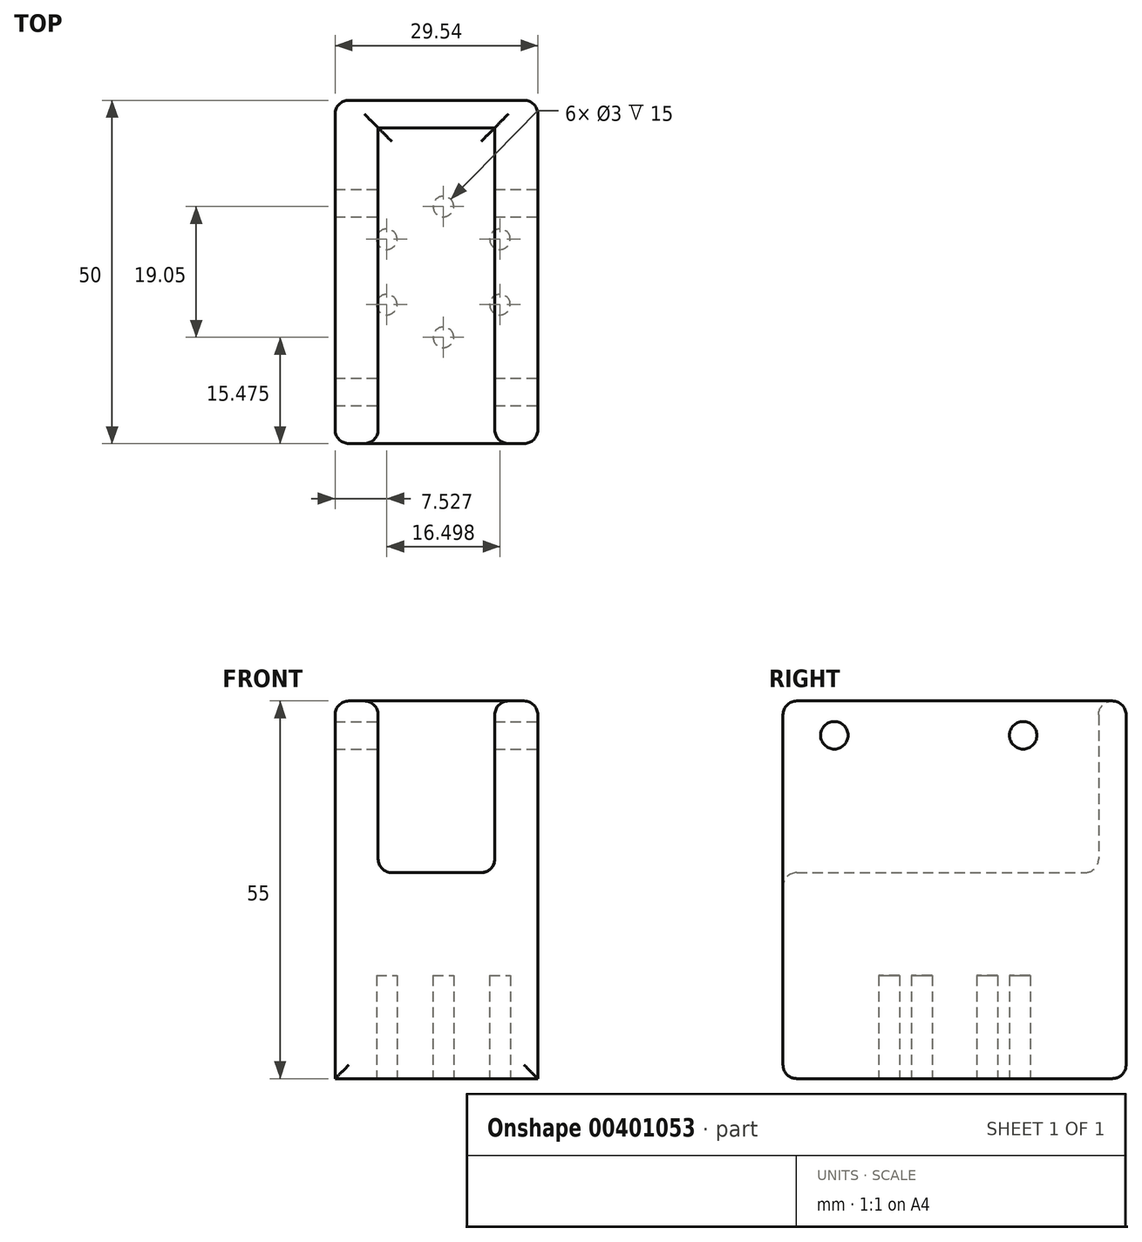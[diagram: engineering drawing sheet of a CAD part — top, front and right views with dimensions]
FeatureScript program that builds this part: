
annotation { "Feature Type Name" : "Feature", "Feature Type Description" : "" }
export const myFeature = defineFeature(function(context is Context, id is Id, definition is map)
    precondition{}
    {
        {
            var Q0;
            Q0=qCreatedBy(makeId("Top.planeOp"),FACE);
            var sketch = newSketch(context, id + "F0", { "sketchPlane" : qUnion([Q0])});
            skLineSegment(sketch, "E0.left", {"start": v(-8.5, 0) * mm, "end": v(-8.5, 21) * mm});
            skLineSegment(sketch, "E0.right", {"start": v(8.5, 0) * mm, "end": v(8.5, 21) * mm});
            skLineSegment(sketch, "E1", {"start": v(-8.5, 21) * mm, "end": v(8.5, 21) * mm});
            skLineSegment(sketch, "E2", {"start": v(8.5, 0) * mm, "end": v(8.5, -23.51) * mm});
            skLineSegment(sketch, "E3", {"start": v(-8.5, 0) * mm, "end": v(-8.5, -23.51) * mm});
            skLineSegment(sketch, "E4", {"start": v(14.77, -13.51) * mm, "end": v(14.77, -20.17) * mm});
            skLineSegment(sketch, "E5.bottom", {"start": v(-25, 25) * mm, "end": v(25, 25) * mm});
            skLineSegment(sketch, "E5.top", {"start": v(-25, -25) * mm, "end": v(25, -25) * mm});
            skLineSegment(sketch, "E5.left", {"start": v(-25, 25) * mm, "end": v(-25, -25) * mm});
            skLineSegment(sketch, "E5.right", {"start": v(25, 25) * mm, "end": v(25, -25) * mm});
            skLineSegment(sketch, "E6", {"start": v(-14.77, -20.17) * mm, "end": v(-14.77, -25) * mm});
            skLineSegment(sketch, "E7", {"start": v(14.77, -20.17) * mm, "end": v(14.77, -25) * mm});
            skLineSegment(sketch, "E8", {"start": v(-8.5, -23.51) * mm, "end": v(-8.5, -25) * mm});
            skLineSegment(sketch, "E9", {"start": v(8.5, -23.51) * mm, "end": v(8.5, -25) * mm});
            skLineSegment(sketch, "E10", {"start": v(14.77, -13.51) * mm, "end": v(14.77, 25) * mm});
            skLineSegment(sketch, "E11", {"start": v(-14.77, -25) * mm, "end": v(-14.77, 25) * mm});
            skSolve(sketch);
        }
        {
            var Q0;
            {var subQ1=sQuery(id+"F0.wireOp",EDGE,"E0.left");Q0=makeQuery(id+"F0.imprint","IMPRINT",FACE,{"disambiguationData":[TD([[makeQuery(id+"F0.imprint","IMPRINT",EDGE,{"derivedFrom":subQ1}),1.0]])]});}
            var Q1;
            {var subQ3=sQuery(id+"F0.wireOp",EDGE,"bu9vcPg2-ATEx-ZIaZ-XLWS-YSRfaz45pnAs");Q1=makeQuery(id+"F0.imprint","IMPRINT",FACE,{"disambiguationData":[TD([[makeQuery(id+"F0.imprint","IMPRINT",EDGE,{"derivedFrom":subQ3}),1.0]])]});}
            var Q2;
            {var subQ4=sQuery(id+"F0.wireOp",EDGE,"E4");Q2=makeQuery(id+"F0.imprint","IMPRINT",FACE,{"disambiguationData":[TD([[makeQuery(id+"F0.imprint","IMPRINT",EDGE,{"derivedFrom":subQ4}),-1.0]])]});}
            extrude(context, id + "F1", {"entities" : qUnion([Q0, Q1, Q2]), "depth" : 25 * mm, "offsetDistance" : 25 * mm});
        }
        {
            var Q0;
            Q0=makeQuery(id+"F0.imprint","IMPRINT",FACE,{"disambiguationData":[TD([[makeQuery(id+"F0.imprint","IMPRINT",EDGE,{"derivedFrom":sQuery(id+"F0.wireOp",EDGE,"JjuJuUTR-XIjw-p3LP-uiln-kea8M6GB0FUg.right")}),-1.0]])]});
            var Q1;
            {var subQ4=sQuery(id+"F0.wireOp",EDGE,"E0.left");Q1=makeQuery(id+"F0.imprint","IMPRINT",FACE,{"disambiguationData":[TD([[makeQuery(id+"F0.imprint","IMPRINT",EDGE,{"derivedFrom":subQ4}),-1.0]])]});}
            var Q2;
            Q2=makeQuery(id+"F0.imprint","IMPRINT",FACE,{"disambiguationData":[TD([[makeQuery(id+"F0.imprint","IMPRINT",EDGE,{"derivedFrom":sQuery(id+"F0.wireOp",EDGE,"JjuJuUTR-XIjw-p3LP-uiln-kea8M6GB0FUg.left")}),1.0]])]});
            var Q3;
            {var subQ1=sQuery(id+"F0.wireOp",EDGE,"E0.left");Q3=makeQuery(id+"F0.imprint","IMPRINT",FACE,{"disambiguationData":[TD([[makeQuery(id+"F0.imprint","IMPRINT",EDGE,{"derivedFrom":subQ1}),1.0]])]});}
            var Q4;
            {var subQ3=sQuery(id+"F0.wireOp",EDGE,"bu9vcPg2-ATEx-ZIaZ-XLWS-YSRfaz45pnAs");Q4=makeQuery(id+"F0.imprint","IMPRINT",FACE,{"disambiguationData":[TD([[makeQuery(id+"F0.imprint","IMPRINT",EDGE,{"derivedFrom":subQ3}),1.0]])]});}
            var Q5;
            {var subQ4=sQuery(id+"F0.wireOp",EDGE,"E4");Q5=makeQuery(id+"F0.imprint","IMPRINT",FACE,{"disambiguationData":[TD([[makeQuery(id+"F0.imprint","IMPRINT",EDGE,{"derivedFrom":subQ4}),-1.0]])]});}
            extrude(context, id + "F2", {"entities" : qUnion([Q0, Q1, Q2, Q3, Q4, Q5]), "operationType" : NewBodyOperationType.ADD, "oppositeDirection" : true, "depth" : 5 * mm, "offsetDistance" : 25 * mm});
        }
        {
            var Q0;
            Q0=makeQuery(id+"F2.opExtrude","CAP_FACE",FACE,{"disambiguationData":[OSD([sQuery(id+"F0.wireOp",EDGE,"E5.bottom"),sQuery(id+"F0.wireOp",EDGE,"E5.top"),sQuery(id+"F0.wireOp",EDGE,"E5.left"),sQuery(id+"F0.wireOp",EDGE,"E5.right")])],"isStart":false});
            extrude(context, id + "F3", {"entities" : qUnion([Q0]), "operationType" : NewBodyOperationType.ADD, "depth" : 25 * mm, "offsetDistance" : 25 * mm});
        }
        {
            var Q0;
            {var subQ0=sQuery(id+"F0.wireOp",EDGE,"E10");var subQ1=sQuery(id+"F0.wireOp",EDGE,"E7");var subQ2=sQuery(id+"F0.wireOp",EDGE,"E4");Q0=makeQuery(id+"F3.boolean.opBoolean","MERGE",FACE,{"derivedFrom":[makeQuery(id+"F2.boolean.opBoolean","MERGE",FACE,{"derivedFrom":[makeQuery(id+"F1.opExtrude","SWEPT_FACE",FACE,{"disambiguationData":[OSD([subQ2,subQ1,subQ0])]}),makeQuery(id+"F2.opExtrude","SWEPT_FACE",FACE,{"disambiguationData":[OSD([subQ2,subQ1,subQ0])]})]}),makeQuery(id+"F3.opExtrude","SWEPT_FACE",FACE,{"disambiguationData":[OSD([subQ2,subQ1,subQ0])]})]});}
            var sketch = newSketch(context, id + "F4", { "sketchPlane" : qUnion([Q0])});
            skCircle(sketch, "E12", {"center": v(10, 20) * mm, "radius": 2 * mm});
            skSolve(sketch);
        }
        {
            var Q0;
            Q0=makeQuery(id+"F4.imprint","IMPRINT",FACE,{"disambiguationData":[TD([[makeQuery(id+"F4.imprint","IMPRINT",EDGE,{"derivedFrom":sQuery(id+"F4.wireOp",EDGE,"E12")}),1.0]])]});
            extrude(context, id + "F5", {"entities" : qUnion([Q0]), "operationType" : NewBodyOperationType.REMOVE, "endBound" : BoundingType.THROUGH_ALL, "oppositeDirection" : true, "depth" : 25 * mm, "offsetDistance" : 25 * mm});
        }
        {
            var Q0;
            Q0=makeQuery(id+"F1.opExtrude","SWEPT_FACE",FACE,{"disambiguationData":[OSD([sQuery(id+"F0.wireOp",EDGE,"E4"),sQuery(id+"F0.wireOp",EDGE,"E7")])]});
            var sketch = newSketch(context, id + "F6", { "sketchPlane" : qUnion([Q0])});
            skCircle(sketch, "E13", {"center": v(-17.51, 20) * mm, "radius": 2 * mm});
            skSolve(sketch);
        }
        {
            var Q0;
            Q0=makeQuery(id+"F6.imprint","IMPRINT",FACE,{"disambiguationData":[TD([[makeQuery(id+"F6.imprint","IMPRINT",EDGE,{"derivedFrom":sQuery(id+"F6.wireOp",EDGE,"E13")}),1.0]])]});
            extrude(context, id + "F7", {"entities" : qUnion([Q0]), "operationType" : NewBodyOperationType.REMOVE, "endBound" : BoundingType.THROUGH_ALL, "oppositeDirection" : true, "depth" : 25 * mm, "offsetDistance" : 25 * mm});
        }
        {
            var Q0;
            {var subQ0=sQuery(id+"F0.wireOp",EDGE,"E5.left");Q0=makeQuery(id+"F3.boolean.opBoolean","MERGE",FACE,{"derivedFrom":[makeQuery(id+"F2.opExtrude","SWEPT_FACE",FACE,{"disambiguationData":[OSD([subQ0])]}),makeQuery(id+"F3.opExtrude","SWEPT_FACE",FACE,{"disambiguationData":[OSD([subQ0])]})]});}
            var Q1;
            Q1=makeQuery(id+"F1.opExtrude","SWEPT_FACE",FACE,{"disambiguationData":[OSD([sQuery(id+"F0.wireOp",EDGE,"cDZ9KRWL-NaUr-2VU4-3PM3-z0CJBz9VJkfU")])]});
            var Q2;
            Q2=makeQuery(id+"F1.opExtrude","CAP_FACE",FACE,{"disambiguationData":[OSD([sQuery(id+"F0.wireOp",EDGE,"E0.left"),sQuery(id+"F0.wireOp",EDGE,"E0.right"),sQuery(id+"F0.wireOp",EDGE,"JjuJuUTR-XIjw-p3LP-uiln-kea8M6GB0FUg.left"),sQuery(id+"F0.wireOp",EDGE,"JjuJuUTR-XIjw-p3LP-uiln-kea8M6GB0FUg.right"),sQuery(id+"F0.wireOp",EDGE,"E1"),sQuery(id+"F0.wireOp",EDGE,"E2"),sQuery(id+"F0.wireOp",EDGE,"E3"),sQuery(id+"F0.wireOp",EDGE,"bu9vcPg2-ATEx-ZIaZ-XLWS-YSRfaz45pnAs"),sQuery(id+"F0.wireOp",EDGE,"E4"),sQuery(id+"F0.wireOp",EDGE,"Vo7dQ3KN-mIEG-PosT-gOyy-nh5kmKhcDDbw"),sQuery(id+"F0.wireOp",EDGE,"1lZYz93q-oRxk-5rwe-9EyB-DwqBscyPRtee"),sQuery(id+"F0.wireOp",EDGE,"E5.bottom"),sQuery(id+"F0.wireOp",EDGE,"E5.top"),sQuery(id+"F0.wireOp",EDGE,"T2WauGqo-VF5D-FPXN-nkIz-Tow7OxX6UALv"),sQuery(id+"F0.wireOp",EDGE,"Eb9nccsw-4lB1-myll-ZeQB-EgrNam2AgwgF"),sQuery(id+"F0.wireOp",EDGE,"E6"),sQuery(id+"F0.wireOp",EDGE,"E7"),sQuery(id+"F0.wireOp",EDGE,"E8"),sQuery(id+"F0.wireOp",EDGE,"E9"),sQuery(id+"F0.wireOp",EDGE,"Qe85SMm2-kEps-NXLD-GZTa-d0BaLbSc7Nne"),sQuery(id+"F0.wireOp",EDGE,"cDZ9KRWL-NaUr-2VU4-3PM3-z0CJBz9VJkfU")])],"isStart":false});
            var Q3;
            {var subQ0=sQuery(id+"F0.wireOp",EDGE,"E5.bottom");Q3=makeQuery(id+"F3.boolean.opBoolean","MERGE",FACE,{"derivedFrom":[makeQuery(id+"F2.boolean.opBoolean","MERGE",FACE,{"derivedFrom":[makeQuery(id+"F1.opExtrude","SWEPT_FACE",FACE,{"disambiguationData":[OSD([subQ0])]}),makeQuery(id+"F2.opExtrude","SWEPT_FACE",FACE,{"disambiguationData":[OSD([subQ0])]})]}),makeQuery(id+"F3.opExtrude","SWEPT_FACE",FACE,{"disambiguationData":[OSD([subQ0])]})]});}
            var Q4;
            Q4=makeQuery(id+"F1.opExtrude","SWEPT_FACE",FACE,{"disambiguationData":[OSD([sQuery(id+"F0.wireOp",EDGE,"Qe85SMm2-kEps-NXLD-GZTa-d0BaLbSc7Nne")])]});
            var Q5;
            {var subQ0=sQuery(id+"F0.wireOp",EDGE,"E5.top");Q5=makeQuery(id+"F3.boolean.opBoolean","MERGE",FACE,{"derivedFrom":[makeQuery(id+"F2.boolean.opBoolean","MERGE",FACE,{"derivedFrom":[makeQuery(id+"F1.opExtrude","SWEPT_FACE",FACE,{"disambiguationData":[OSD([subQ0]),TDD([makeQuery(id+"F0.imprint","IMPRINT",EDGE,{"disambiguationData":[TD([[makeQuery(id+"F0.imprint","INTERSECT",VERTEX,{"derivedFrom":[subQ0,sQuery(id+"F0.wireOp",EDGE,"E6")]}),-1.0]])],"derivedFrom":subQ0})])]}),makeQuery(id+"F1.opExtrude","SWEPT_FACE",FACE,{"disambiguationData":[OSD([subQ0]),TDD([makeQuery(id+"F0.imprint","IMPRINT",EDGE,{"disambiguationData":[TD([[makeQuery(id+"F0.imprint","INTERSECT",VERTEX,{"derivedFrom":[subQ0,sQuery(id+"F0.wireOp",EDGE,"E7")]}),1.0]])],"derivedFrom":subQ0})])]}),makeQuery(id+"F2.opExtrude","SWEPT_FACE",FACE,{"disambiguationData":[OSD([subQ0])]})]}),makeQuery(id+"F3.opExtrude","SWEPT_FACE",FACE,{"disambiguationData":[OSD([subQ0])]})]});}
            var Q6;
            {var subQ1=sQuery(id+"F0.wireOp",EDGE,"E5.top");var subQ2=sQuery(id+"F0.wireOp",EDGE,"E5.bottom");var subQ3=sQuery(id+"F0.wireOp",EDGE,"E5.left");Q6=makeQuery(id+"F2.boolean.opBoolean","SPLIT",FACE,{"disambiguationData":[TD([makeQuery(id+"F1.opExtrude","SWEPT_FACE",FACE,{"disambiguationData":[OSD([sQuery(id+"F0.wireOp",EDGE,"cDZ9KRWL-NaUr-2VU4-3PM3-z0CJBz9VJkfU")])]})])],"derivedFrom":makeQuery(id+"F2.opExtrude","CAP_FACE",FACE,{"disambiguationData":[OSD([subQ2,subQ1,subQ3,sQuery(id+"F0.wireOp",EDGE,"E5.right")])],"isStart":true})});}
            var Q7;
            {var subQ0=sQuery(id+"F0.wireOp",EDGE,"E5.bottom");var subQ1=sQuery(id+"F0.wireOp",EDGE,"E5.right");var subQ3=sQuery(id+"F0.wireOp",EDGE,"E5.top");Q7=makeQuery(id+"F2.boolean.opBoolean","SPLIT",FACE,{"disambiguationData":[TD([makeQuery(id+"F1.opExtrude","SWEPT_FACE",FACE,{"disambiguationData":[OSD([sQuery(id+"F0.wireOp",EDGE,"Qe85SMm2-kEps-NXLD-GZTa-d0BaLbSc7Nne")])]})])],"derivedFrom":makeQuery(id+"F2.opExtrude","CAP_FACE",FACE,{"disambiguationData":[OSD([subQ0,subQ3,sQuery(id+"F0.wireOp",EDGE,"E5.left"),subQ1])],"isStart":true})});}
            fillet(context, id + "F8", {"entities" : qUnion([Q0, Q1, Q2, Q3, Q4, Q5, Q6, Q7]), "radius" : 2 * mm, "tangentPropagation" : true, "allowEdgeOverflow" : false});
        }
        {
            var Q0;
            Q0=makeQuery(id+"F3.opExtrude","CAP_FACE",FACE,{"disambiguationData":[OSD([sQuery(id+"F0.wireOp",EDGE,"E5.bottom"),sQuery(id+"F0.wireOp",EDGE,"E5.top"),sQuery(id+"F0.wireOp",EDGE,"E5.left"),sQuery(id+"F0.wireOp",EDGE,"E5.right")])],"isStart":false});
            var sketch = newSketch(context, id + "F9", { "sketchPlane" : qUnion([Q0])});
            skCircle(sketch, "E14", {"center": v(1, 9.53) * mm, "radius": 1.5 * mm});
            skCircle(sketch, "E15.1.0", {"center": v(-7.24, 4.76) * mm, "radius": 1.5 * mm});
            skCircle(sketch, "E15.2.0", {"center": v(-7.24, -4.76) * mm, "radius": 1.5 * mm});
            skCircle(sketch, "E15.3.0", {"center": v(1, -9.53) * mm, "radius": 1.5 * mm});
            skCircle(sketch, "E15.4.0", {"center": v(9.25, -4.76) * mm, "radius": 1.5 * mm});
            skCircle(sketch, "E15.5.0", {"center": v(9.25, 4.76) * mm, "radius": 1.5 * mm});
            skPoint(sketch, "E15.center", {"position": v(1, 0) * mm});
            skSolve(sketch);
        }
        {
            var Q0;
            Q0=makeQuery(id+"F9.imprint","IMPRINT",FACE,{"disambiguationData":[TD([[makeQuery(id+"F9.imprint","IMPRINT",EDGE,{"derivedFrom":sQuery(id+"F9.wireOp",EDGE,"E15.4.0")}),1.0]])]});
            var Q1;
            Q1=makeQuery(id+"F9.imprint","IMPRINT",FACE,{"disambiguationData":[TD([[makeQuery(id+"F9.imprint","IMPRINT",EDGE,{"derivedFrom":sQuery(id+"F9.wireOp",EDGE,"E15.3.0")}),1.0]])]});
            var Q2;
            Q2=makeQuery(id+"F9.imprint","IMPRINT",FACE,{"disambiguationData":[TD([[makeQuery(id+"F9.imprint","IMPRINT",EDGE,{"derivedFrom":sQuery(id+"F9.wireOp",EDGE,"E15.2.0")}),1.0]])]});
            var Q3;
            Q3=makeQuery(id+"F9.imprint","IMPRINT",FACE,{"disambiguationData":[TD([[makeQuery(id+"F9.imprint","IMPRINT",EDGE,{"derivedFrom":sQuery(id+"F9.wireOp",EDGE,"E15.1.0")}),1.0]])]});
            var Q4;
            Q4=makeQuery(id+"F9.imprint","IMPRINT",FACE,{"disambiguationData":[TD([[makeQuery(id+"F9.imprint","IMPRINT",EDGE,{"derivedFrom":sQuery(id+"F9.wireOp",EDGE,"E14")}),1.0]])]});
            var Q5;
            Q5=makeQuery(id+"F9.imprint","IMPRINT",FACE,{"disambiguationData":[TD([[makeQuery(id+"F9.imprint","IMPRINT",EDGE,{"derivedFrom":sQuery(id+"F9.wireOp",EDGE,"E15.5.0")}),1.0]])]});
            extrude(context, id + "F10", {"entities" : qUnion([Q0, Q1, Q2, Q3, Q4, Q5]), "operationType" : NewBodyOperationType.REMOVE, "oppositeDirection" : true, "depth" : 15 * mm, "offsetDistance" : 25 * mm});
        }
    });
